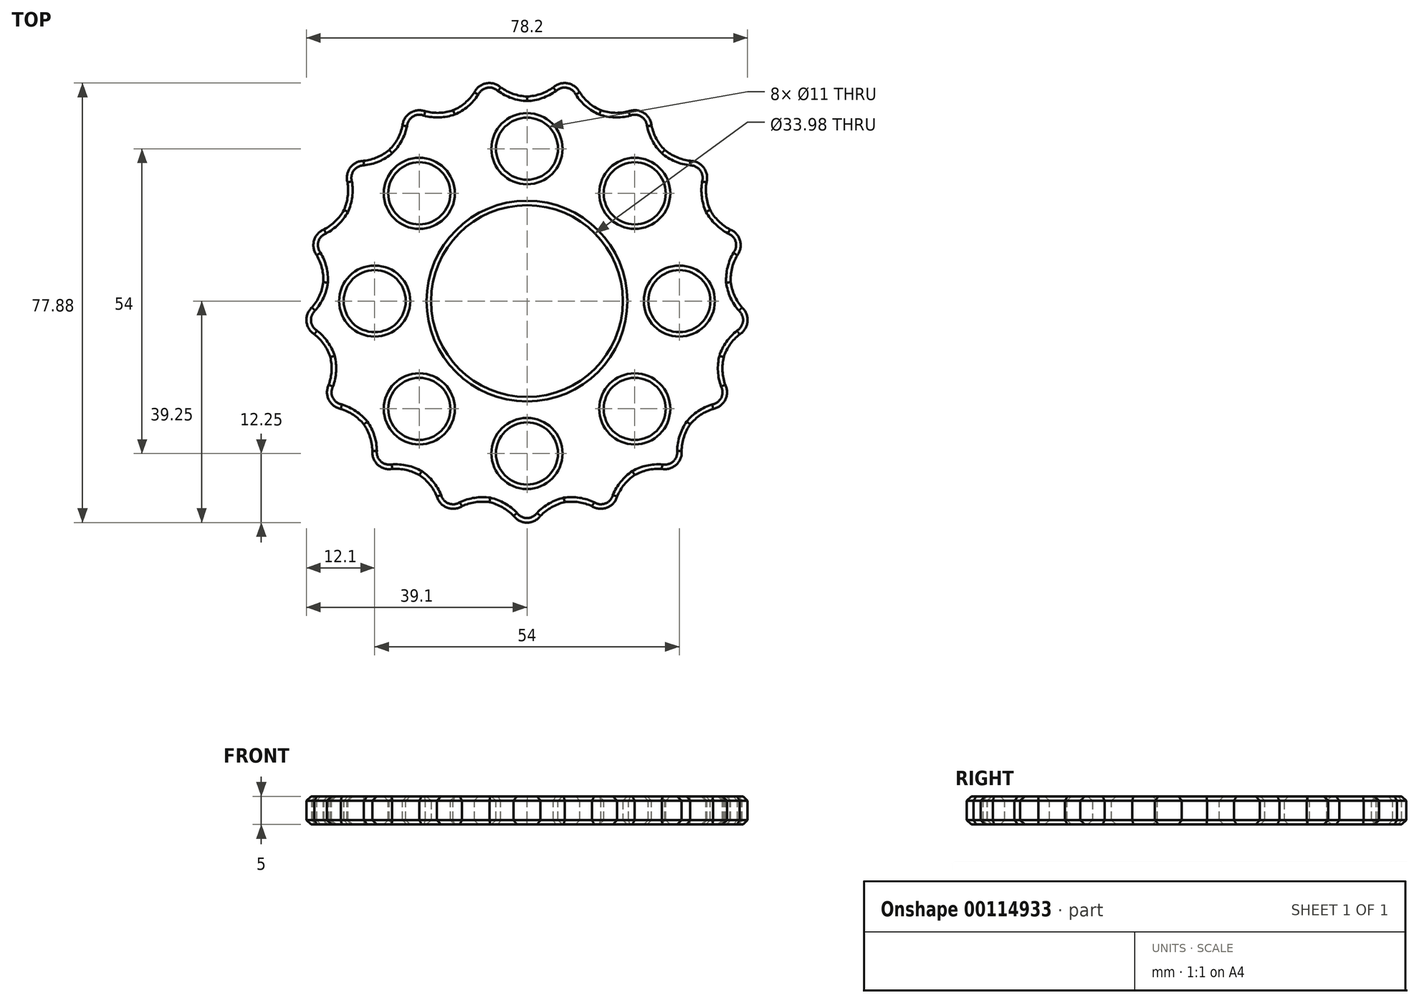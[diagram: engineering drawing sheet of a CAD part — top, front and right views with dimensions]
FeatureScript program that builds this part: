
annotation { "Feature Type Name" : "Feature", "Feature Type Description" : "" }
export const myFeature = defineFeature(function(context is Context, id is Id, definition is map)
    precondition{}
    {
        {
            var Q0;
            Q0=qCreatedBy(makeId("Top.planeOp"),FACE);
            var sketch = newSketch(context, id + "F0", { "sketchPlane" : qUnion([Q0])});
            skCircle(sketch, "E0", {"center": v(0, 0) * mm, "radius": 16.99 * mm});
            skCircle(sketch, "E1", {"center": v(0, 0) * mm, "radius": 39.25 * mm});
            skSolve(sketch);
        }
        {
            var Q0;
            Q0=makeQuery(id+"F0.imprint","IMPRINT",FACE,{"disambiguationData":[TD([[makeQuery(id+"F0.imprint","IMPRINT",EDGE,{"derivedFrom":sQuery(id+"F0.wireOp",EDGE,"E0")}),-1.0]])]});
            extrude(context, id + "F1", {"entities" : qUnion([Q0]), "depth" : 5 * mm});
        }
        {
            var Q0;
            Q0=makeQuery(id+"F1.opExtrude","CAP_FACE",FACE,{"disambiguationData":[OSD([sQuery(id+"F0.wireOp",EDGE,"E0"),sQuery(id+"F0.wireOp",EDGE,"E1")])],"isStart":false});
            var sketch = newSketch(context, id + "F2", { "sketchPlane" : qUnion([Q0])});
            skPoint(sketch, "E2.center", {"position": v(0, 0) * mm});
            skCircle(sketch, "E3", {"center": v(27, 0) * mm, "radius": 5.5 * mm});
            skCircle(sketch, "E4.1.0", {"center": v(19.1, 19.1) * mm, "radius": 5.5 * mm});
            skCircle(sketch, "E4.2.0", {"center": v(0, 27) * mm, "radius": 5.5 * mm});
            skCircle(sketch, "E4.3.0", {"center": v(-19.1, 19.1) * mm, "radius": 5.5 * mm});
            skCircle(sketch, "E4.4.0", {"center": v(-27, 0) * mm, "radius": 5.5 * mm});
            skCircle(sketch, "E4.5.0", {"center": v(-19.1, -19.1) * mm, "radius": 5.5 * mm});
            skCircle(sketch, "E4.6.0", {"center": v(0, -27) * mm, "radius": 5.5 * mm});
            skCircle(sketch, "E4.7.0", {"center": v(19.1, -19.1) * mm, "radius": 5.5 * mm});
            skSolve(sketch);
        }
        {
            var Q0;
            Q0 = qSketchRegion(id + "F2", true);
            extrude(context, id + "F3", {"entities" : qUnion([Q0]), "operationType" : NewBodyOperationType.REMOVE, "oppositeDirection" : true, "depth" : 25 * mm});
        }
        {
            var Q0;
            Q0=makeQuery(id+"F1.opExtrude","CAP_FACE",FACE,{"disambiguationData":[OSD([sQuery(id+"F0.wireOp",EDGE,"E0"),sQuery(id+"F0.wireOp",EDGE,"E1")])],"isStart":false});
            var sketch = newSketch(context, id + "F4", { "sketchPlane" : qUnion([Q0])});
            skCircle(sketch, "E5", {"center": v(0, 0) * mm, "radius": 36.25 * mm});
            skLineSegment(sketch, "E6", {"start": v(0, 18.12) * mm, "end": v(0, 36.25) * mm});
            skLineSegment(sketch, "E7", {"start": v(6.66, 35.63) * mm, "end": v(7.21, 38.58) * mm});
            skCircle(sketch, "E8", {"center": v(0, 0) * mm, "radius": 39.25 * mm});
            skLineSegment(sketch, "E9.1.0", {"start": v(19.08, 30.82) * mm, "end": v(20.66, 33.37) * mm});
            skLineSegment(sketch, "E9.2.0", {"start": v(28.93, 21.85) * mm, "end": v(31.32, 23.65) * mm});
            skLineSegment(sketch, "E9.3.0", {"start": v(34.87, 9.92) * mm, "end": v(37.75, 10.74) * mm});
            skLineSegment(sketch, "E9.4.0", {"start": v(36.1, -3.34) * mm, "end": v(39.08, -3.62) * mm});
            skLineSegment(sketch, "E9.5.0", {"start": v(32.45, -16.16) * mm, "end": v(35.14, -17.5) * mm});
            skLineSegment(sketch, "E9.8.0", {"start": v(0, -36.25) * mm, "end": v(0, -39.25) * mm});
            skLineSegment(sketch, "E9.9.0", {"start": v(-13.1, -33.8) * mm, "end": v(-14.18, -36.6) * mm});
            skLineSegment(sketch, "E9.10.0", {"start": v(-24.42, -26.79) * mm, "end": v(-26.44, -29) * mm});
            skLineSegment(sketch, "E9.11.0", {"start": v(-32.45, -16.16) * mm, "end": v(-35.14, -17.5) * mm});
            skLineSegment(sketch, "E9.12.0", {"start": v(-36.1, -3.34) * mm, "end": v(-39.08, -3.62) * mm});
            skLineSegment(sketch, "E9.13.0", {"start": v(-34.87, 9.92) * mm, "end": v(-37.75, 10.74) * mm});
            skLineSegment(sketch, "E9.14.0", {"start": v(-28.93, 21.85) * mm, "end": v(-31.32, 23.65) * mm});
            skLineSegment(sketch, "E9.15.0", {"start": v(-19.08, 30.82) * mm, "end": v(-20.66, 33.37) * mm});
            skLineSegment(sketch, "E9.16.0", {"start": v(-6.66, 35.63) * mm, "end": v(-7.21, 38.58) * mm});
            skLineSegment(sketch, "E9.anchor1", {"start": v(0, 0) * mm, "end": v(0, 0) * mm});
            skLineSegment(sketch, "E9.anchor2", {"start": v(0, 0) * mm, "end": v(0, 0) * mm});
            skPoint(sketch, "E10.endSnap0", {"position": v(0, 18.12) * mm});
            skPoint(sketch, "E10.end.orphan", {"position": v(3.67, 18.12) * mm});
            skPoint(sketch, "E10.start.orphan", {"position": v(0, 18.12) * mm});
            skLineSegment(sketch, "E11.1.0", {"start": v(-6.55, 16.9) * mm, "end": v(-13.1, 33.8) * mm});
            skLineSegment(sketch, "E11.2.0", {"start": v(-12.21, 13.4) * mm, "end": v(-24.42, 26.79) * mm});
            skLineSegment(sketch, "E11.3.0", {"start": v(-16.22, 8.08) * mm, "end": v(-32.45, 16.16) * mm});
            skLineSegment(sketch, "E11.4.0", {"start": v(-18.05, 1.67) * mm, "end": v(-36.1, 3.34) * mm});
            skLineSegment(sketch, "E11.5.0", {"start": v(-17.43, -4.96) * mm, "end": v(-34.87, -9.92) * mm});
            skLineSegment(sketch, "E11.6.0", {"start": v(-14.46, -10.92) * mm, "end": v(-28.93, -21.85) * mm});
            skLineSegment(sketch, "E11.7.0", {"start": v(-9.54, -15.41) * mm, "end": v(-19.08, -30.82) * mm});
            skLineSegment(sketch, "E11.8.0", {"start": v(-3.33, -17.82) * mm, "end": v(-6.66, -35.63) * mm});
            skLineSegment(sketch, "E11.9.0", {"start": v(3.33, -17.82) * mm, "end": v(6.66, -35.63) * mm});
            skLineSegment(sketch, "E11.10.0", {"start": v(9.54, -15.41) * mm, "end": v(19.08, -30.82) * mm});
            skLineSegment(sketch, "E11.11.0", {"start": v(14.46, -10.92) * mm, "end": v(28.93, -21.85) * mm});
            skLineSegment(sketch, "E11.12.0", {"start": v(17.43, -4.96) * mm, "end": v(34.87, -9.92) * mm});
            skLineSegment(sketch, "E11.13.0", {"start": v(18.05, 1.67) * mm, "end": v(36.1, 3.34) * mm});
            skLineSegment(sketch, "E11.14.0", {"start": v(16.22, 8.08) * mm, "end": v(32.45, 16.16) * mm});
            skLineSegment(sketch, "E11.15.0", {"start": v(12.21, 13.4) * mm, "end": v(24.42, 26.79) * mm});
            skLineSegment(sketch, "E11.16.0", {"start": v(6.55, 16.9) * mm, "end": v(13.1, 33.8) * mm});
            skCircle(sketch, "E12", {"center": v(0, 0) * mm, "radius": 49.99 * mm});
            skArc(sketch, "E13", {"start": v(-2.39, -38.07) * mm, "mid": v(0, -39.25) * mm, "end": v(2.39, -38.07) * mm});
            skArc(sketch, "E14.1.0", {"start": v(11.52, -36.36) * mm, "mid": v(14.18, -36.6) * mm, "end": v(15.98, -34.63) * mm});
            skArc(sketch, "E14.2.0", {"start": v(23.88, -29.74) * mm, "mid": v(26.44, -29) * mm, "end": v(27.4, -26.52) * mm});
            skCircle(sketch, "E14.3.0", {"center": v(32.45, -16.16) * mm, "radius": 3 * mm});
            skCircle(sketch, "E14.4.0", {"center": v(36.1, -3.34) * mm, "radius": 3 * mm});
            skCircle(sketch, "E14.5.0", {"center": v(34.87, 9.92) * mm, "radius": 3 * mm});
            skCircle(sketch, "E14.6.0", {"center": v(28.93, 21.85) * mm, "radius": 3 * mm});
            skCircle(sketch, "E14.7.0", {"center": v(19.08, 30.82) * mm, "radius": 3 * mm});
            skCircle(sketch, "E14.8.0", {"center": v(6.66, 35.63) * mm, "radius": 3 * mm});
            skCircle(sketch, "E14.9.0", {"center": v(-6.66, 35.63) * mm, "radius": 3 * mm});
            skCircle(sketch, "E14.10.0", {"center": v(-19.08, 30.82) * mm, "radius": 3 * mm});
            skCircle(sketch, "E14.11.0", {"center": v(-28.93, 21.85) * mm, "radius": 3 * mm});
            skCircle(sketch, "E14.12.0", {"center": v(-34.87, 9.92) * mm, "radius": 3 * mm});
            skCircle(sketch, "E14.13.0", {"center": v(-36.1, -3.34) * mm, "radius": 3 * mm});
            skCircle(sketch, "E14.14.0", {"center": v(-32.45, -16.16) * mm, "radius": 3 * mm});
            skCircle(sketch, "E14.15.0", {"center": v(-24.42, -26.79) * mm, "radius": 3 * mm});
            skCircle(sketch, "E14.16.0", {"center": v(-13.1, -33.8) * mm, "radius": 3 * mm});
            skArc(sketch, "E15", {"start": v(7.06, -35.59) * mm, "mid": v(6.66, -35.63) * mm, "end": v(6.27, -35.73) * mm});
            skArc(sketch, "E16", {"start": v(6.66, -35.63) * mm, "mid": v(4.35, -36.54) * mm, "end": v(2.39, -38.07) * mm});
            skArc(sketch, "E17.MirrorCS", {"start": v(6.66, -35.63) * mm, "mid": v(9.15, -35.64) * mm, "end": v(11.53, -36.36) * mm});
            skArc(sketch, "E18.1.0", {"start": v(19.08, -30.82) * mm, "mid": v(21.4, -29.93) * mm, "end": v(23.88, -29.74) * mm});
            skArc(sketch, "E18.1.1", {"start": v(19.08, -30.82) * mm, "mid": v(17.25, -32.5) * mm, "end": v(15.98, -34.63) * mm});
            skArc(sketch, "E18.2.0", {"start": v(28.93, -21.85) * mm, "mid": v(30.77, -20.18) * mm, "end": v(33.01, -19.1) * mm});
            skArc(sketch, "E18.2.1", {"start": v(28.93, -21.85) * mm, "mid": v(27.83, -24.07) * mm, "end": v(27.4, -26.52) * mm});
            skArc(sketch, "E18.3.0", {"start": v(34.87, -9.92) * mm, "mid": v(35.98, -7.7) * mm, "end": v(37.68, -5.89) * mm});
            skArc(sketch, "E18.3.1", {"start": v(34.87, -9.92) * mm, "mid": v(34.65, -12.4) * mm, "end": v(35.14, -14.83) * mm});
            skArc(sketch, "E18.4.0", {"start": v(36.1, 3.34) * mm, "mid": v(36.33, 5.82) * mm, "end": v(37.27, 8.12) * mm});
            skArc(sketch, "E18.4.1", {"start": v(36.1, 3.34) * mm, "mid": v(36.78, 0.96) * mm, "end": v(38.13, -1.14) * mm});
            skArc(sketch, "E18.5.0", {"start": v(32.45, 16.16) * mm, "mid": v(31.78, 18.55) * mm, "end": v(31.82, 21.04) * mm});
            skArc(sketch, "E18.5.1", {"start": v(32.45, 16.16) * mm, "mid": v(33.95, 14.18) * mm, "end": v(35.96, 12.71) * mm});
            skArc(sketch, "E18.6.0", {"start": v(24.42, 26.79) * mm, "mid": v(22.93, 28.78) * mm, "end": v(22.07, 31.1) * mm});
            skArc(sketch, "E18.6.1", {"start": v(24.42, 26.79) * mm, "mid": v(26.54, 25.49) * mm, "end": v(28.94, 24.85) * mm});
            skArc(sketch, "E18.7.0", {"start": v(13.1, 33.8) * mm, "mid": v(10.99, 35.12) * mm, "end": v(9.34, 36.98) * mm});
            skArc(sketch, "E18.7.1", {"start": v(13.1, 33.8) * mm, "mid": v(15.54, 33.35) * mm, "end": v(18.01, 33.62) * mm});
            skArc(sketch, "E18.8.0", {"start": v(0, 36.25) * mm, "mid": v(-2.44, 36.72) * mm, "end": v(-4.65, 37.86) * mm});
            skArc(sketch, "E18.8.1", {"start": v(0, 36.25) * mm, "mid": v(2.44, 36.72) * mm, "end": v(4.65, 37.86) * mm});
            skArc(sketch, "E18.9.0", {"start": v(-13.1, 33.8) * mm, "mid": v(-15.54, 33.35) * mm, "end": v(-18.01, 33.62) * mm});
            skArc(sketch, "E18.9.1", {"start": v(-13.1, 33.8) * mm, "mid": v(-10.99, 35.12) * mm, "end": v(-9.34, 36.98) * mm});
            skArc(sketch, "E18.10.0", {"start": v(-24.42, 26.79) * mm, "mid": v(-26.54, 25.49) * mm, "end": v(-28.94, 24.85) * mm});
            skArc(sketch, "E18.10.1", {"start": v(-24.42, 26.79) * mm, "mid": v(-22.93, 28.78) * mm, "end": v(-22.07, 31.1) * mm});
            skArc(sketch, "E18.11.0", {"start": v(-32.45, 16.16) * mm, "mid": v(-33.95, 14.18) * mm, "end": v(-35.96, 12.71) * mm});
            skArc(sketch, "E18.11.1", {"start": v(-32.45, 16.16) * mm, "mid": v(-31.78, 18.55) * mm, "end": v(-31.82, 21.04) * mm});
            skArc(sketch, "E18.12.0", {"start": v(-36.1, 3.34) * mm, "mid": v(-36.78, 0.96) * mm, "end": v(-38.13, -1.14) * mm});
            skArc(sketch, "E18.12.1", {"start": v(-36.1, 3.34) * mm, "mid": v(-36.33, 5.82) * mm, "end": v(-37.27, 8.12) * mm});
            skArc(sketch, "E18.13.0", {"start": v(-34.87, -9.92) * mm, "mid": v(-34.65, -12.4) * mm, "end": v(-35.14, -14.83) * mm});
            skArc(sketch, "E18.13.1", {"start": v(-34.87, -9.92) * mm, "mid": v(-35.98, -7.7) * mm, "end": v(-37.68, -5.89) * mm});
            skArc(sketch, "E18.14.0", {"start": v(-28.93, -21.85) * mm, "mid": v(-27.83, -24.07) * mm, "end": v(-27.4, -26.52) * mm});
            skArc(sketch, "E18.14.1", {"start": v(-28.93, -21.85) * mm, "mid": v(-30.77, -20.18) * mm, "end": v(-33.01, -19.1) * mm});
            skArc(sketch, "E18.15.0", {"start": v(-19.08, -30.82) * mm, "mid": v(-17.25, -32.5) * mm, "end": v(-15.98, -34.63) * mm});
            skArc(sketch, "E18.15.1", {"start": v(-19.08, -30.82) * mm, "mid": v(-21.4, -29.93) * mm, "end": v(-23.88, -29.74) * mm});
            skArc(sketch, "E18.16.0", {"start": v(-6.66, -35.63) * mm, "mid": v(-4.35, -36.54) * mm, "end": v(-2.39, -38.07) * mm});
            skArc(sketch, "E18.16.1", {"start": v(-6.66, -35.63) * mm, "mid": v(-9.15, -35.64) * mm, "end": v(-11.53, -36.36) * mm});
            skSolve(sketch);
        }
        {
            var Q0;
            {var subQ0=sQuery(id+"F4.wireOp",EDGE,"E17.MirrorCS");var subQ1=sQuery(id+"F4.wireOp",EDGE,"E14.1.0");var subQ2=makeQuery(id+"F4.imprint","INTERSECT",VERTEX,{"derivedFrom":[subQ1,subQ0]});Q0=makeQuery(id+"F4.imprint","IMPRINT",FACE,{"disambiguationData":[TD([[makeQuery(id+"F4.imprint","IMPRINT",EDGE,{"disambiguationData":[TD([[subQ2,-1.0]])],"derivedFrom":subQ1}),-1.0]])]});}
            var Q1;
            {var subQ5=sQuery(id+"F4.wireOp",EDGE,"E18.1.1");Q1=makeQuery(id+"F4.imprint","IMPRINT",FACE,{"disambiguationData":[TD([[makeQuery(id+"F4.imprint","IMPRINT",EDGE,{"derivedFrom":subQ5}),1.0]])]});}
            var Q2;
            {var subQ0=sQuery(id+"F4.wireOp",EDGE,"E18.2.1");Q2=makeQuery(id+"F4.imprint","IMPRINT",FACE,{"disambiguationData":[TD([[makeQuery(id+"F4.imprint","IMPRINT",EDGE,{"derivedFrom":subQ0}),1.0]])]});}
            var Q3;
            {var subQ7=sQuery(id+"F4.wireOp",EDGE,"E18.3.1");Q3=makeQuery(id+"F4.imprint","IMPRINT",FACE,{"disambiguationData":[TD([[makeQuery(id+"F4.imprint","IMPRINT",EDGE,{"derivedFrom":subQ7}),1.0]])]});}
            var Q4;
            {var subQ7=sQuery(id+"F4.wireOp",EDGE,"E18.4.1");Q4=makeQuery(id+"F4.imprint","IMPRINT",FACE,{"disambiguationData":[TD([[makeQuery(id+"F4.imprint","IMPRINT",EDGE,{"derivedFrom":subQ7}),1.0]])]});}
            var Q5;
            {var subQ8=sQuery(id+"F4.wireOp",EDGE,"E18.5.1");Q5=makeQuery(id+"F4.imprint","IMPRINT",FACE,{"disambiguationData":[TD([[makeQuery(id+"F4.imprint","IMPRINT",EDGE,{"derivedFrom":subQ8}),1.0]])]});}
            var Q6;
            {var subQ8=sQuery(id+"F4.wireOp",EDGE,"E18.6.1");Q6=makeQuery(id+"F4.imprint","IMPRINT",FACE,{"disambiguationData":[TD([[makeQuery(id+"F4.imprint","IMPRINT",EDGE,{"derivedFrom":subQ8}),1.0]])]});}
            var Q7;
            {var subQ8=sQuery(id+"F4.wireOp",EDGE,"E18.7.1");Q7=makeQuery(id+"F4.imprint","IMPRINT",FACE,{"disambiguationData":[TD([[makeQuery(id+"F4.imprint","IMPRINT",EDGE,{"derivedFrom":subQ8}),1.0]])]});}
            var Q8;
            {var subQ4=sQuery(id+"F4.wireOp",EDGE,"E18.8.1");Q8=makeQuery(id+"F4.imprint","IMPRINT",FACE,{"disambiguationData":[TD([[makeQuery(id+"F4.imprint","IMPRINT",EDGE,{"derivedFrom":subQ4}),1.0]])]});}
            var Q9;
            {var subQ4=sQuery(id+"F4.wireOp",EDGE,"E18.9.1");Q9=makeQuery(id+"F4.imprint","IMPRINT",FACE,{"disambiguationData":[TD([[makeQuery(id+"F4.imprint","IMPRINT",EDGE,{"derivedFrom":subQ4}),1.0]])]});}
            var Q10;
            {var subQ8=sQuery(id+"F4.wireOp",EDGE,"E18.10.1");Q10=makeQuery(id+"F4.imprint","IMPRINT",FACE,{"disambiguationData":[TD([[makeQuery(id+"F4.imprint","IMPRINT",EDGE,{"derivedFrom":subQ8}),1.0]])]});}
            var Q11;
            {var subQ4=sQuery(id+"F4.wireOp",EDGE,"E18.11.1");Q11=makeQuery(id+"F4.imprint","IMPRINT",FACE,{"disambiguationData":[TD([[makeQuery(id+"F4.imprint","IMPRINT",EDGE,{"derivedFrom":subQ4}),1.0]])]});}
            var Q12;
            {var subQ6=sQuery(id+"F4.wireOp",EDGE,"E18.12.1");Q12=makeQuery(id+"F4.imprint","IMPRINT",FACE,{"disambiguationData":[TD([[makeQuery(id+"F4.imprint","IMPRINT",EDGE,{"derivedFrom":subQ6}),1.0]])]});}
            var Q13;
            {var subQ8=sQuery(id+"F4.wireOp",EDGE,"E18.13.1");Q13=makeQuery(id+"F4.imprint","IMPRINT",FACE,{"disambiguationData":[TD([[makeQuery(id+"F4.imprint","IMPRINT",EDGE,{"derivedFrom":subQ8}),1.0]])]});}
            var Q14;
            {var subQ6=sQuery(id+"F4.wireOp",EDGE,"E18.14.1");Q14=makeQuery(id+"F4.imprint","IMPRINT",FACE,{"disambiguationData":[TD([[makeQuery(id+"F4.imprint","IMPRINT",EDGE,{"derivedFrom":subQ6}),1.0]])]});}
            var Q15;
            {var subQ4=sQuery(id+"F4.wireOp",EDGE,"E18.15.1");Q15=makeQuery(id+"F4.imprint","IMPRINT",FACE,{"disambiguationData":[TD([[makeQuery(id+"F4.imprint","IMPRINT",EDGE,{"derivedFrom":subQ4}),1.0]])]});}
            var Q16;
            {var subQ0=sQuery(id+"F4.wireOp",EDGE,"E18.16.1");Q16=makeQuery(id+"F4.imprint","IMPRINT",FACE,{"disambiguationData":[TD([[makeQuery(id+"F4.imprint","IMPRINT",EDGE,{"derivedFrom":subQ0}),1.0]])]});}
            extrude(context, id + "F5", {"entities" : qUnion([Q0, Q1, Q2, Q3, Q4, Q5, Q6, Q7, Q8, Q9, Q10, Q11, Q12, Q13, Q14, Q15, Q16]), "operationType" : NewBodyOperationType.REMOVE, "oppositeDirection" : true, "depth" : 25 * mm});
        }
        {
            var Q0;
            Q0=makeQuery(id+"F1.opExtrude","CAP_FACE",FACE,{"disambiguationData":[OSD([sQuery(id+"F0.wireOp",EDGE,"E0"),sQuery(id+"F0.wireOp",EDGE,"E1")])],"isStart":false});
            var Q1;
            Q1=makeQuery(id+"F1.opExtrude","CAP_FACE",FACE,{"disambiguationData":[OSD([sQuery(id+"F0.wireOp",EDGE,"E0"),sQuery(id+"F0.wireOp",EDGE,"E1")])],"isStart":true});
            chamfer(context, id + "F6", {"entities" : qUnion([Q0, Q1]), "width" : .8 * mm, "tangentPropagation" : true});
        }
    });
